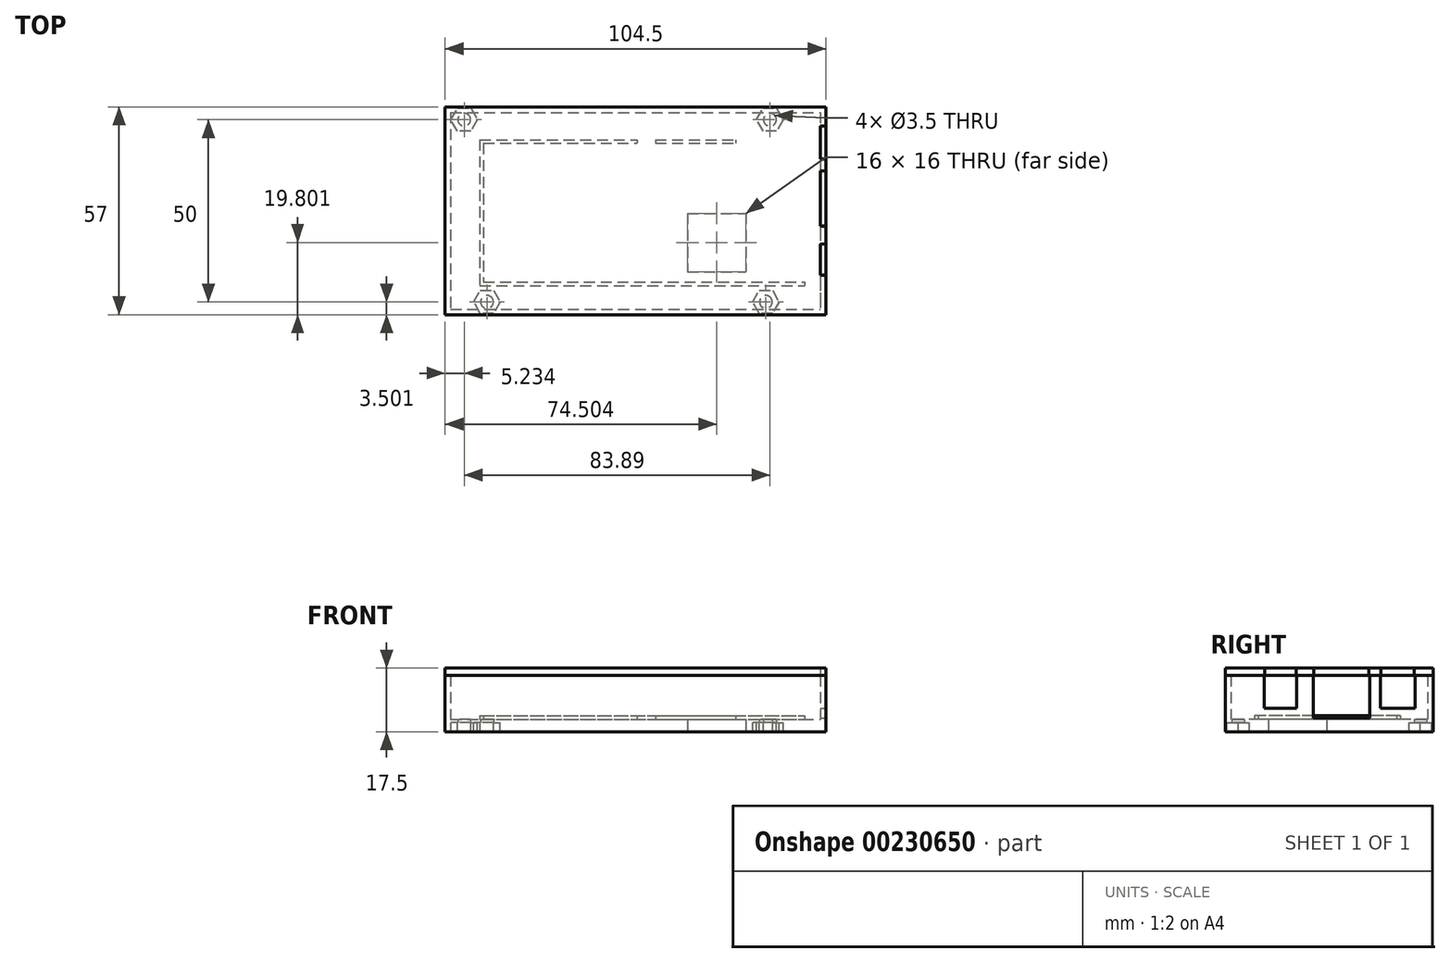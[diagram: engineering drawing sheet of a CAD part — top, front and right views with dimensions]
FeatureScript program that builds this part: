
annotation { "Feature Type Name" : "Feature", "Feature Type Description" : "" }
export const myFeature = defineFeature(function(context is Context, id is Id, definition is map)
    precondition{}
    {
        {
            var Q0;
            Q0=qCreatedBy(makeId("Top.planeOp"),FACE);
            var sketch = newSketch(context, id + "F0", { "sketchPlane" : qUnion([Q0])});
            skLineSegment(sketch, "E0.bottom", {"start": v(-51.77, 19.57) * mm, "end": v(52.73, 19.57) * mm});
            skLineSegment(sketch, "E0.top", {"start": v(-51.77, -37.43) * mm, "end": v(52.73, -37.43) * mm});
            skLineSegment(sketch, "E0.left", {"start": v(-51.77, 19.57) * mm, "end": v(-51.77, -37.43) * mm});
            skLineSegment(sketch, "E0.right", {"start": v(52.73, 19.57) * mm, "end": v(52.73, -37.43) * mm});
            skLineSegment(sketch, "E1.0", {"start": v(-50.27, 18.07) * mm, "end": v(51.23, 18.07) * mm});
            skLineSegment(sketch, "E2.0", {"start": v(-50.27, -35.93) * mm, "end": v(51.23, -35.93) * mm});
            skLineSegment(sketch, "E3.0", {"start": v(51.23, 18.07) * mm, "end": v(51.23, -35.93) * mm});
            skLineSegment(sketch, "E4.0", {"start": v(-50.27, 18.07) * mm, "end": v(-50.27, -35.93) * mm});
            skLineSegment(sketch, "E5.0", {"start": v(14.73, -25.63) * mm, "end": v(30.73, -25.63) * mm});
            skLineSegment(sketch, "E6.0", {"start": v(14.73, -9.63) * mm, "end": v(30.73, -9.63) * mm});
            skLineSegment(sketch, "E7.0", {"start": v(30.73, -9.63) * mm, "end": v(30.73, -25.63) * mm});
            skLineSegment(sketch, "E8.0", {"start": v(14.73, -9.63) * mm, "end": v(14.73, -25.63) * mm});
            skLineSegment(sketch, "E9.0", {"start": v(-42.27, -29.43) * mm, "end": v(46.93, -29.43) * mm});
            skLineSegment(sketch, "E10.0", {"start": v(-42.27, 10.57) * mm, "end": v(-42.27, -29.43) * mm});
            skLineSegment(sketch, "E11.0", {"start": v(-42.27, 10.57) * mm, "end": v(0.93, 10.57) * mm});
            skLineSegment(sketch, "E12.0", {"start": v(0.93, 10.57) * mm, "end": v(0.93, 9.57) * mm});
            skLineSegment(sketch, "E13.0", {"start": v(5.93, 10.57) * mm, "end": v(5.93, 9.57) * mm});
            skLineSegment(sketch, "E14.0", {"start": v(27.93, 10.57) * mm, "end": v(27.93, 9.57) * mm});
            skLineSegment(sketch, "E15.trimOffspring", {"start": v(5.93, 10.57) * mm, "end": v(27.93, 10.57) * mm});
            skLineSegment(sketch, "E16.trimOffspring", {"start": v(5.93, 9.57) * mm, "end": v(27.93, 9.57) * mm});
            skLineSegment(sketch, "E17", {"start": v(51.23, 18.07) * mm, "end": v(52.73, 18.07) * mm});
            skLineSegment(sketch, "E18.0", {"start": v(51.23, 14.57) * mm, "end": v(52.73, 14.57) * mm});
            skLineSegment(sketch, "E19.0", {"start": v(51.23, 5.07) * mm, "end": v(52.73, 5.07) * mm});
            skLineSegment(sketch, "E20.0", {"start": v(51.23, 2.17) * mm, "end": v(52.73, 2.17) * mm});
            skLineSegment(sketch, "E21.0", {"start": v(51.23, -0.83) * mm, "end": v(52.73, -0.83) * mm});
            skLineSegment(sketch, "E22.0", {"start": v(51.23, -8.83) * mm, "end": v(52.73, -8.83) * mm});
            skLineSegment(sketch, "E23.0", {"start": v(51.23, -13.33) * mm, "end": v(52.73, -13.33) * mm});
            skLineSegment(sketch, "E24.0", {"start": v(51.23, -17.83) * mm, "end": v(52.73, -17.83) * mm});
            skLineSegment(sketch, "E25.0", {"start": v(51.23, -26.83) * mm, "end": v(52.73, -26.83) * mm});
            skLineSegment(sketch, "E26.0", {"start": v(36.23, 16.07) * mm, "end": v(36.23, -34.93) * mm, "construction": true});
            skLineSegment(sketch, "E27.0", {"start": v(-48.77, -33.93) * mm, "end": v(51.23, -33.93) * mm});
            skLineSegment(sketch, "E28.0", {"start": v(37.35, 16.07) * mm, "end": v(37.35, -34.93) * mm, "construction": true});
            skLineSegment(sketch, "E29.0", {"start": v(-46.54, 18.07) * mm, "end": v(-46.54, -34.93) * mm, "construction": true});
            skLineSegment(sketch, "E30.0", {"start": v(-40.27, 17.07) * mm, "end": v(-40.27, -35.93) * mm, "construction": true});
            skLineSegment(sketch, "E31.0", {"start": v(-48.77, 16.07) * mm, "end": v(51.23, 16.07) * mm, "construction": true});
            skCircle(sketch, "E32", {"center": v(36.23, -33.93) * mm, "radius": 1.75 * mm});
            skCircle(sketch, "E33", {"center": v(37.35, 16.07) * mm, "radius": 1.75 * mm});
            skCircle(sketch, "E34", {"center": v(-46.54, 16.07) * mm, "radius": 1.75 * mm});
            skCircle(sketch, "E35", {"center": v(-40.27, -33.93) * mm, "radius": 1.75 * mm});
            skLineSegment(sketch, "E36.0", {"start": v(-41.27, 9.57) * mm, "end": v(-41.27, -28.43) * mm});
            skLineSegment(sketch, "E37.trimOffspring", {"start": v(-41.27, 9.57) * mm, "end": v(0.93, 9.57) * mm});
            skLineSegment(sketch, "E38.trimOffspring", {"start": v(-41.27, -28.43) * mm, "end": v(46.93, -28.43) * mm});
            skCircle(sketch, "E39.cCircle", {"center": v(-40.27, -33.93) * mm, "radius": 3.15 * mm, "construction": true});
            skLineSegment(sketch, "E39.0", {"start": v(-42.08, -30.78) * mm, "end": v(-38.45, -30.78) * mm});
            skLineSegment(sketch, "E39.1", {"start": v(-38.45, -30.78) * mm, "end": v(-36.63, -33.93) * mm});
            skLineSegment(sketch, "E39.2", {"start": v(-36.63, -33.93) * mm, "end": v(-38.45, -37.08) * mm});
            skLineSegment(sketch, "E39.3", {"start": v(-38.45, -37.08) * mm, "end": v(-42.08, -37.08) * mm});
            skLineSegment(sketch, "E39.4", {"start": v(-42.08, -37.08) * mm, "end": v(-43.9, -33.93) * mm});
            skLineSegment(sketch, "E39.5", {"start": v(-43.9, -33.93) * mm, "end": v(-42.08, -30.78) * mm});
            skPoint(sketch, "E39.0.midPoint", {"position": v(-40.27, -30.78) * mm});
            skCircle(sketch, "E40.cCircle", {"center": v(36.23, -33.93) * mm, "radius": 3.15 * mm, "construction": true});
            skLineSegment(sketch, "E40.0", {"start": v(34.42, -30.78) * mm, "end": v(38.05, -30.78) * mm});
            skLineSegment(sketch, "E40.1", {"start": v(38.05, -30.78) * mm, "end": v(39.87, -33.93) * mm});
            skLineSegment(sketch, "E40.2", {"start": v(39.87, -33.93) * mm, "end": v(38.05, -37.08) * mm});
            skLineSegment(sketch, "E40.3", {"start": v(38.05, -37.08) * mm, "end": v(34.42, -37.08) * mm});
            skLineSegment(sketch, "E40.4", {"start": v(34.42, -37.08) * mm, "end": v(32.6, -33.93) * mm});
            skLineSegment(sketch, "E40.5", {"start": v(32.6, -33.93) * mm, "end": v(34.42, -30.78) * mm});
            skPoint(sketch, "E40.0.midPoint", {"position": v(36.23, -30.78) * mm});
            skCircle(sketch, "E41.cCircle", {"center": v(-46.54, 16.07) * mm, "radius": 3.15 * mm, "construction": true});
            skLineSegment(sketch, "E41.0", {"start": v(-44.72, 12.92) * mm, "end": v(-48.35, 12.92) * mm});
            skLineSegment(sketch, "E41.1", {"start": v(-48.35, 12.92) * mm, "end": v(-50.17, 16.07) * mm});
            skLineSegment(sketch, "E41.2", {"start": v(-50.17, 16.07) * mm, "end": v(-48.35, 19.22) * mm});
            skLineSegment(sketch, "E41.3", {"start": v(-48.35, 19.22) * mm, "end": v(-44.72, 19.22) * mm});
            skLineSegment(sketch, "E41.4", {"start": v(-44.72, 19.22) * mm, "end": v(-42.9, 16.07) * mm});
            skLineSegment(sketch, "E41.5", {"start": v(-42.9, 16.07) * mm, "end": v(-44.72, 12.92) * mm});
            skPoint(sketch, "E41.0.midPoint", {"position": v(-46.54, 12.92) * mm});
            skCircle(sketch, "E42.cCircle", {"center": v(37.35, 16.07) * mm, "radius": 3.15 * mm, "construction": true});
            skLineSegment(sketch, "E42.0", {"start": v(39.17, 12.92) * mm, "end": v(35.54, 12.92) * mm});
            skLineSegment(sketch, "E42.1", {"start": v(35.54, 12.92) * mm, "end": v(33.72, 16.07) * mm});
            skLineSegment(sketch, "E42.2", {"start": v(33.72, 16.07) * mm, "end": v(35.54, 19.22) * mm});
            skLineSegment(sketch, "E42.3", {"start": v(35.54, 19.22) * mm, "end": v(39.17, 19.22) * mm});
            skLineSegment(sketch, "E42.4", {"start": v(39.17, 19.22) * mm, "end": v(41, 16.07) * mm});
            skLineSegment(sketch, "E42.5", {"start": v(41, 16.07) * mm, "end": v(39.17, 12.92) * mm});
            skPoint(sketch, "E42.0.midPoint", {"position": v(37.35, 12.92) * mm});
            skLineSegment(sketch, "E43", {"start": v(46.93, -28.43) * mm, "end": v(46.93, -29.43) * mm});
            skLineSegment(sketch, "E44", {"start": v(-51.77, -8.93) * mm, "end": v(-50.27, -8.93) * mm, "construction": true});
            skLineSegment(sketch, "E45", {"start": v(-50.27, -8.93) * mm, "end": v(-42.27, -9.43) * mm, "construction": true});
            skLineSegment(sketch, "E46", {"start": v(-42.27, -9.43) * mm, "end": v(-41.27, -9.43) * mm, "construction": true});
            skLineSegment(sketch, "E47", {"start": v(-41.27, -9.43) * mm, "end": v(-40.27, -9.43) * mm, "construction": true});
            skLineSegment(sketch, "E48", {"start": v(-40.27, -9.43) * mm, "end": v(36.23, -9.43) * mm, "construction": true});
            skLineSegment(sketch, "E49", {"start": v(36.23, -9.43) * mm, "end": v(37.35, -9.43) * mm, "construction": true});
            skSolve(sketch);
        }
        {
            var Q0;
            {var subQ1=sQuery(id+"F0.wireOp",EDGE,"E1.0");Q0=makeQuery(id+"F0.imprint","IMPRINT",FACE,{"disambiguationData":[TD([[makeQuery(id+"F0.imprint","IMPRINT",EDGE,{"derivedFrom":subQ1}),-1.0]])]});}
            var Q1;
            Q1=makeQuery(id+"F0.imprint","IMPRINT",FACE,{"disambiguationData":[TD([[makeQuery(id+"F0.imprint","IMPRINT",EDGE,{"derivedFrom":sQuery(id+"F0.wireOp",EDGE,"E34")}),-1.0]])]});
            var Q2;
            Q2=makeQuery(id+"F0.imprint","IMPRINT",FACE,{"disambiguationData":[TD([[makeQuery(id+"F0.imprint","IMPRINT",EDGE,{"derivedFrom":sQuery(id+"F0.wireOp",EDGE,"E33")}),-1.0]])]});
            var Q3;
            {var subQ5=sQuery(id+"F0.wireOp",EDGE,"E40.4");var subQ8=sQuery(id+"F0.wireOp",EDGE,"E2.0");var subQ9=makeQuery(id+"F0.imprint","INTERSECT",VERTEX,{"derivedFrom":[subQ8,subQ5]});Q3=makeQuery(id+"F0.imprint","IMPRINT",FACE,{"disambiguationData":[TD([[makeQuery(id+"F0.imprint","IMPRINT",EDGE,{"disambiguationData":[TD([[subQ9,-1.0]])],"derivedFrom":subQ8}),1.0]])]});}
            var Q4;
            Q4=makeQuery(id+"F0.imprint","IMPRINT",FACE,{"disambiguationData":[TD([[makeQuery(id+"F0.imprint","IMPRINT",EDGE,{"derivedFrom":sQuery(id+"F0.wireOp",EDGE,"E40.0")}),-1.0]])]});
            var Q5;
            {var subQ6=sQuery(id+"F0.wireOp",EDGE,"E39.4");var subQ8=sQuery(id+"F0.wireOp",EDGE,"E2.0");var subQ9=makeQuery(id+"F0.imprint","INTERSECT",VERTEX,{"derivedFrom":[subQ8,subQ6]});Q5=makeQuery(id+"F0.imprint","IMPRINT",FACE,{"disambiguationData":[TD([[makeQuery(id+"F0.imprint","IMPRINT",EDGE,{"disambiguationData":[TD([[subQ9,-1.0]])],"derivedFrom":subQ8}),1.0]])]});}
            var Q6;
            Q6=makeQuery(id+"F0.imprint","IMPRINT",FACE,{"disambiguationData":[TD([[makeQuery(id+"F0.imprint","IMPRINT",EDGE,{"derivedFrom":sQuery(id+"F0.wireOp",EDGE,"E39.0")}),-1.0]])]});
            var Q7;
            {var subQ0=sQuery(id+"F0.wireOp",EDGE,"E4.0");var subQ1=sQuery(id+"F0.wireOp",EDGE,"E2.0");var subQ2=makeQuery(id+"F0.imprint","INTERSECT",VERTEX,{"derivedFrom":[subQ1,subQ0]});Q7=makeQuery(id+"F0.imprint","IMPRINT",FACE,{"disambiguationData":[TD([[makeQuery(id+"F0.imprint","IMPRINT",EDGE,{"disambiguationData":[TD([[subQ2,-1.0]])],"derivedFrom":subQ1}),1.0]])]});}
            var Q8;
            {var subQ0=sQuery(id+"F0.wireOp",EDGE,"E39.2");var subQ1=sQuery(id+"F0.wireOp",EDGE,"E2.0");var subQ2=makeQuery(id+"F0.imprint","INTERSECT",VERTEX,{"derivedFrom":[subQ1,subQ0]});Q8=makeQuery(id+"F0.imprint","IMPRINT",FACE,{"disambiguationData":[TD([[makeQuery(id+"F0.imprint","IMPRINT",EDGE,{"disambiguationData":[TD([[subQ2,-1.0]])],"derivedFrom":subQ1}),1.0]])]});}
            var Q9;
            {var subQ0=sQuery(id+"F0.wireOp",EDGE,"E3.0");var subQ1=sQuery(id+"F0.wireOp",EDGE,"E2.0");var subQ2=makeQuery(id+"F0.imprint","INTERSECT",VERTEX,{"derivedFrom":[subQ1,subQ0]});Q9=makeQuery(id+"F0.imprint","IMPRINT",FACE,{"disambiguationData":[TD([[makeQuery(id+"F0.imprint","IMPRINT",EDGE,{"disambiguationData":[TD([[subQ2,1.0]])],"derivedFrom":subQ1}),1.0]])]});}
            extrude(context, id + "F1", {"entities" : qUnion([Q0, Q1, Q2, Q3, Q4, Q5, Q6, Q7, Q8, Q9]), "depth" : 1 * mm});
        }
        {
            var Q0;
            {var subQ1=sQuery(id+"F0.wireOp",EDGE,"E9.0");Q0=makeQuery(id+"F0.imprint","IMPRINT",FACE,{"disambiguationData":[TD([[makeQuery(id+"F0.imprint","IMPRINT",EDGE,{"derivedFrom":subQ1}),1.0]])]});}
            var Q1;
            Q1=makeQuery(id+"F0.imprint","IMPRINT",FACE,{"disambiguationData":[TD([[makeQuery(id+"F0.imprint","IMPRINT",EDGE,{"derivedFrom":sQuery(id+"F0.wireOp",EDGE,"E13.0")}),1.0]])]});
            extrude(context, id + "F2", {"entities" : qUnion([Q0, Q1]), "operationType" : NewBodyOperationType.ADD, "depth" : 2 * mm});
        }
        {
            var Q0;
            {var subQ4=sQuery(id+"F0.wireOp",EDGE,"E0.bottom");Q0=makeQuery(id+"F0.imprint","IMPRINT",FACE,{"disambiguationData":[TD([[makeQuery(id+"F0.imprint","IMPRINT",EDGE,{"derivedFrom":subQ4}),-1.0]])]});}
            var Q1;
            {var subQ0=sQuery(id+"F0.wireOp",EDGE,"E17");Q1=makeQuery(id+"F0.imprint","IMPRINT",FACE,{"disambiguationData":[TD([[makeQuery(id+"F0.imprint","IMPRINT",EDGE,{"derivedFrom":subQ0}),-1.0]])]});}
            var Q2;
            {var subQ0=sQuery(id+"F0.wireOp",EDGE,"E19.0");Q2=makeQuery(id+"F0.imprint","IMPRINT",FACE,{"disambiguationData":[TD([[makeQuery(id+"F0.imprint","IMPRINT",EDGE,{"derivedFrom":subQ0}),-1.0]])]});}
            var Q3;
            {var subQ0=sQuery(id+"F0.wireOp",EDGE,"E23.0");Q3=makeQuery(id+"F0.imprint","IMPRINT",FACE,{"disambiguationData":[TD([[makeQuery(id+"F0.imprint","IMPRINT",EDGE,{"derivedFrom":subQ0}),-1.0]])]});}
            var Q4;
            {var subQ5=sQuery(id+"F0.wireOp",EDGE,"E40.3");Q4=makeQuery(id+"F0.imprint","IMPRINT",FACE,{"disambiguationData":[TD([[makeQuery(id+"F0.imprint","IMPRINT",EDGE,{"derivedFrom":subQ5}),-1.0]])]});}
            var Q5;
            {var subQ5=sQuery(id+"F0.wireOp",EDGE,"E39.3");Q5=makeQuery(id+"F0.imprint","IMPRINT",FACE,{"disambiguationData":[TD([[makeQuery(id+"F0.imprint","IMPRINT",EDGE,{"derivedFrom":subQ5}),-1.0]])]});}
            var Q6;
            {var subQ5=sQuery(id+"F0.wireOp",EDGE,"E42.3");Q6=makeQuery(id+"F0.imprint","IMPRINT",FACE,{"disambiguationData":[TD([[makeQuery(id+"F0.imprint","IMPRINT",EDGE,{"derivedFrom":subQ5}),-1.0]])]});}
            var Q7;
            {var subQ5=sQuery(id+"F0.wireOp",EDGE,"E41.3");Q7=makeQuery(id+"F0.imprint","IMPRINT",FACE,{"disambiguationData":[TD([[makeQuery(id+"F0.imprint","IMPRINT",EDGE,{"derivedFrom":subQ5}),-1.0]])]});}
            extrude(context, id + "F3", {"entities" : qUnion([Q0, Q1, Q2, Q3, Q4, Q5, Q6, Q7]), "operationType" : NewBodyOperationType.ADD, "depth" : 13 * mm});
        }
        {
            var Q0;
            {var subQ0=sQuery(id+"F0.wireOp",EDGE,"E18.0");Q0=makeQuery(id+"F0.imprint","IMPRINT",FACE,{"disambiguationData":[TD([[makeQuery(id+"F0.imprint","IMPRINT",EDGE,{"derivedFrom":subQ0}),-1.0]])]});}
            var Q1;
            {var subQ0=sQuery(id+"F0.wireOp",EDGE,"E24.0");Q1=makeQuery(id+"F0.imprint","IMPRINT",FACE,{"disambiguationData":[TD([[makeQuery(id+"F0.imprint","IMPRINT",EDGE,{"derivedFrom":subQ0}),-1.0]])]});}
            extrude(context, id + "F4", {"entities" : qUnion([Q0, Q1]), "operationType" : NewBodyOperationType.ADD, "depth" : 4 * mm});
        }
        {
            var Q0;
            {var subQ0=sQuery(id+"F0.wireOp",EDGE,"E20.0");Q0=makeQuery(id+"F0.imprint","IMPRINT",FACE,{"disambiguationData":[TD([[makeQuery(id+"F0.imprint","IMPRINT",EDGE,{"derivedFrom":subQ0}),-1.0]])]});}
            var Q1;
            {var subQ0=sQuery(id+"F0.wireOp",EDGE,"E21.0");Q1=makeQuery(id+"F0.imprint","IMPRINT",FACE,{"disambiguationData":[TD([[makeQuery(id+"F0.imprint","IMPRINT",EDGE,{"derivedFrom":subQ0}),-1.0]])]});}
            var Q2;
            {var subQ0=sQuery(id+"F0.wireOp",EDGE,"E22.0");Q2=makeQuery(id+"F0.imprint","IMPRINT",FACE,{"disambiguationData":[TD([[makeQuery(id+"F0.imprint","IMPRINT",EDGE,{"derivedFrom":subQ0}),-1.0]])]});}
            extrude(context, id + "F5", {"entities" : qUnion([Q0, Q1, Q2]), "operationType" : NewBodyOperationType.ADD, "depth" : 1.3 * mm, "offsetDistance" : 25 * mm});
        }
        {
            var Q0;
            {var subQ23=sQuery(id+"F0.wireOp",EDGE,"E0.bottom");Q0=makeQuery(id+"F0.imprint","IMPRINT",FACE,{"disambiguationData":[TD([[makeQuery(id+"F0.imprint","IMPRINT",EDGE,{"derivedFrom":subQ23}),-1.0]])]});}
            var Q1;
            {var subQ0=sQuery(id+"F0.wireOp",EDGE,"E17");Q1=makeQuery(id+"F0.imprint","IMPRINT",FACE,{"disambiguationData":[TD([[makeQuery(id+"F0.imprint","IMPRINT",EDGE,{"derivedFrom":subQ0}),-1.0]])]});}
            var Q2;
            {var subQ0=sQuery(id+"F0.wireOp",EDGE,"E18.0");Q2=makeQuery(id+"F0.imprint","IMPRINT",FACE,{"disambiguationData":[TD([[makeQuery(id+"F0.imprint","IMPRINT",EDGE,{"derivedFrom":subQ0}),-1.0]])]});}
            var Q3;
            {var subQ0=sQuery(id+"F0.wireOp",EDGE,"E19.0");Q3=makeQuery(id+"F0.imprint","IMPRINT",FACE,{"disambiguationData":[TD([[makeQuery(id+"F0.imprint","IMPRINT",EDGE,{"derivedFrom":subQ0}),-1.0]])]});}
            var Q4;
            {var subQ0=sQuery(id+"F0.wireOp",EDGE,"E20.0");Q4=makeQuery(id+"F0.imprint","IMPRINT",FACE,{"disambiguationData":[TD([[makeQuery(id+"F0.imprint","IMPRINT",EDGE,{"derivedFrom":subQ0}),-1.0]])]});}
            var Q5;
            {var subQ0=sQuery(id+"F0.wireOp",EDGE,"E21.0");Q5=makeQuery(id+"F0.imprint","IMPRINT",FACE,{"disambiguationData":[TD([[makeQuery(id+"F0.imprint","IMPRINT",EDGE,{"derivedFrom":subQ0}),-1.0]])]});}
            var Q6;
            {var subQ0=sQuery(id+"F0.wireOp",EDGE,"E22.0");Q6=makeQuery(id+"F0.imprint","IMPRINT",FACE,{"disambiguationData":[TD([[makeQuery(id+"F0.imprint","IMPRINT",EDGE,{"derivedFrom":subQ0}),-1.0]])]});}
            var Q7;
            {var subQ0=sQuery(id+"F0.wireOp",EDGE,"E23.0");Q7=makeQuery(id+"F0.imprint","IMPRINT",FACE,{"disambiguationData":[TD([[makeQuery(id+"F0.imprint","IMPRINT",EDGE,{"derivedFrom":subQ0}),-1.0]])]});}
            var Q8;
            {var subQ0=sQuery(id+"F0.wireOp",EDGE,"E24.0");Q8=makeQuery(id+"F0.imprint","IMPRINT",FACE,{"disambiguationData":[TD([[makeQuery(id+"F0.imprint","IMPRINT",EDGE,{"derivedFrom":subQ0}),-1.0]])]});}
            var Q9;
            {var subQ0=sQuery(id+"F0.wireOp",EDGE,"E3.0");var subQ1=sQuery(id+"F0.wireOp",EDGE,"E2.0");var subQ2=makeQuery(id+"F0.imprint","INTERSECT",VERTEX,{"derivedFrom":[subQ1,subQ0]});Q9=makeQuery(id+"F0.imprint","IMPRINT",FACE,{"disambiguationData":[TD([[makeQuery(id+"F0.imprint","IMPRINT",EDGE,{"disambiguationData":[TD([[subQ2,1.0]])],"derivedFrom":subQ1}),1.0]])]});}
            var Q10;
            {var subQ0=sQuery(id+"F0.wireOp",EDGE,"E39.2");var subQ1=sQuery(id+"F0.wireOp",EDGE,"E2.0");var subQ2=makeQuery(id+"F0.imprint","INTERSECT",VERTEX,{"derivedFrom":[subQ1,subQ0]});Q10=makeQuery(id+"F0.imprint","IMPRINT",FACE,{"disambiguationData":[TD([[makeQuery(id+"F0.imprint","IMPRINT",EDGE,{"disambiguationData":[TD([[subQ2,-1.0]])],"derivedFrom":subQ1}),1.0]])]});}
            var Q11;
            {var subQ0=sQuery(id+"F0.wireOp",EDGE,"E4.0");var subQ1=sQuery(id+"F0.wireOp",EDGE,"E2.0");var subQ2=makeQuery(id+"F0.imprint","INTERSECT",VERTEX,{"derivedFrom":[subQ1,subQ0]});Q11=makeQuery(id+"F0.imprint","IMPRINT",FACE,{"disambiguationData":[TD([[makeQuery(id+"F0.imprint","IMPRINT",EDGE,{"disambiguationData":[TD([[subQ2,-1.0]])],"derivedFrom":subQ1}),1.0]])]});}
            var Q12;
            Q12=makeQuery(id+"F0.imprint","IMPRINT",FACE,{"disambiguationData":[TD([[makeQuery(id+"F0.imprint","IMPRINT",EDGE,{"derivedFrom":sQuery(id+"F0.wireOp",EDGE,"E5.0")}),-1.0]])]});
            var Q13;
            Q13=makeQuery(id+"F0.imprint","IMPRINT",FACE,{"disambiguationData":[TD([[makeQuery(id+"F0.imprint","IMPRINT",EDGE,{"derivedFrom":sQuery(id+"F0.wireOp",EDGE,"E13.0")}),1.0]])]});
            var Q14;
            Q14=makeQuery(id+"F0.imprint","IMPRINT",FACE,{"disambiguationData":[TD([[makeQuery(id+"F0.imprint","IMPRINT",EDGE,{"derivedFrom":sQuery(id+"F0.wireOp",EDGE,"E9.0")}),1.0]])]});
            extrude(context, id + "F6", {"entities" : qUnion([Q0, Q1, Q2, Q3, Q4, Q5, Q6, Q7, Q8, Q9, Q10, Q11, Q12, Q13, Q14]), "operationType" : NewBodyOperationType.ADD, "oppositeDirection" : true, "depth" : 2.5 * mm});
        }
        {
            var Q0;
            Q0=makeQuery(id+"F3.opExtrude","CAP_FACE",FACE,{"disambiguationData":[OSD([sQuery(id+"F0.wireOp",EDGE,"E0.bottom"),sQuery(id+"F0.wireOp",EDGE,"E0.top"),sQuery(id+"F0.wireOp",EDGE,"E0.left"),sQuery(id+"F0.wireOp",EDGE,"E0.right"),sQuery(id+"F0.wireOp",EDGE,"E1.0"),sQuery(id+"F0.wireOp",EDGE,"E2.0"),sQuery(id+"F0.wireOp",EDGE,"E3.0"),sQuery(id+"F0.wireOp",EDGE,"E4.0"),sQuery(id+"F0.wireOp",EDGE,"E18.0"),sQuery(id+"F0.wireOp",EDGE,"E25.0")])],"isStart":false});
            var sketch = newSketch(context, id + "F7", { "sketchPlane" : qUnion([Q0])});
            skLineSegment(sketch, "E50.bottom", {"start": v(-51.77, 19.57) * mm, "end": v(52.73, 19.57) * mm});
            skLineSegment(sketch, "E50.top", {"start": v(-51.77, -37.43) * mm, "end": v(52.73, -37.43) * mm});
            skLineSegment(sketch, "E50.left", {"start": v(-51.77, 19.57) * mm, "end": v(-51.77, -37.43) * mm});
            skLineSegment(sketch, "E50.right", {"start": v(52.73, 19.57) * mm, "end": v(52.73, -37.43) * mm});
            skLineSegment(sketch, "E51.0", {"start": v(51.23, 14.37) * mm, "end": v(52.73, 14.37) * mm});
            skLineSegment(sketch, "E52.0", {"start": v(51.23, 5.27) * mm, "end": v(52.73, 5.27) * mm});
            skLineSegment(sketch, "E53.0", {"start": v(51.23, 1.97) * mm, "end": v(52.73, 1.97) * mm});
            skLineSegment(sketch, "E54.0", {"start": v(51.23, -13.13) * mm, "end": v(52.73, -13.13) * mm});
            skLineSegment(sketch, "E55.0", {"start": v(51.23, -18.03) * mm, "end": v(52.73, -18.03) * mm});
            skLineSegment(sketch, "E56.0", {"start": v(51.23, -26.63) * mm, "end": v(52.73, -26.63) * mm});
            skLineSegment(sketch, "E57.left", {"start": v(51.23, 14.37) * mm, "end": v(51.23, 5.27) * mm});
            skLineSegment(sketch, "E57.right", {"start": v(52.73, 14.37) * mm, "end": v(52.73, 5.27) * mm});
            skLineSegment(sketch, "E58.left", {"start": v(51.23, 1.97) * mm, "end": v(51.23, -13.13) * mm});
            skLineSegment(sketch, "E58.right", {"start": v(52.73, 1.97) * mm, "end": v(52.73, -13.13) * mm});
            skLineSegment(sketch, "E59.left", {"start": v(51.23, -18.03) * mm, "end": v(51.23, -26.63) * mm});
            skLineSegment(sketch, "E59.right", {"start": v(52.73, -18.03) * mm, "end": v(52.73, -26.63) * mm});
            skSolve(sketch);
        }
        {
            var Q0;
            {var subQ2=sQuery(id+"F7.wireOp",EDGE,"E51.0");Q0=makeQuery(id+"F7.imprint","IMPRINT",FACE,{"disambiguationData":[TD([[makeQuery(id+"F7.imprint","IMPRINT",EDGE,{"derivedFrom":subQ2}),1.0]])]});}
            var Q1;
            {var subQ6=sQuery(id+"F7.wireOp",EDGE,"E50.bottom");Q1=makeQuery(id+"F7.imprint","IMPRINT",FACE,{"disambiguationData":[TD([[makeQuery(id+"F7.imprint","IMPRINT",EDGE,{"derivedFrom":subQ6}),-1.0]])]});}
            extrude(context, id + "F8", {"entities" : qUnion([Q0, Q1]), "depth" : 2 * mm});
        }
    });
